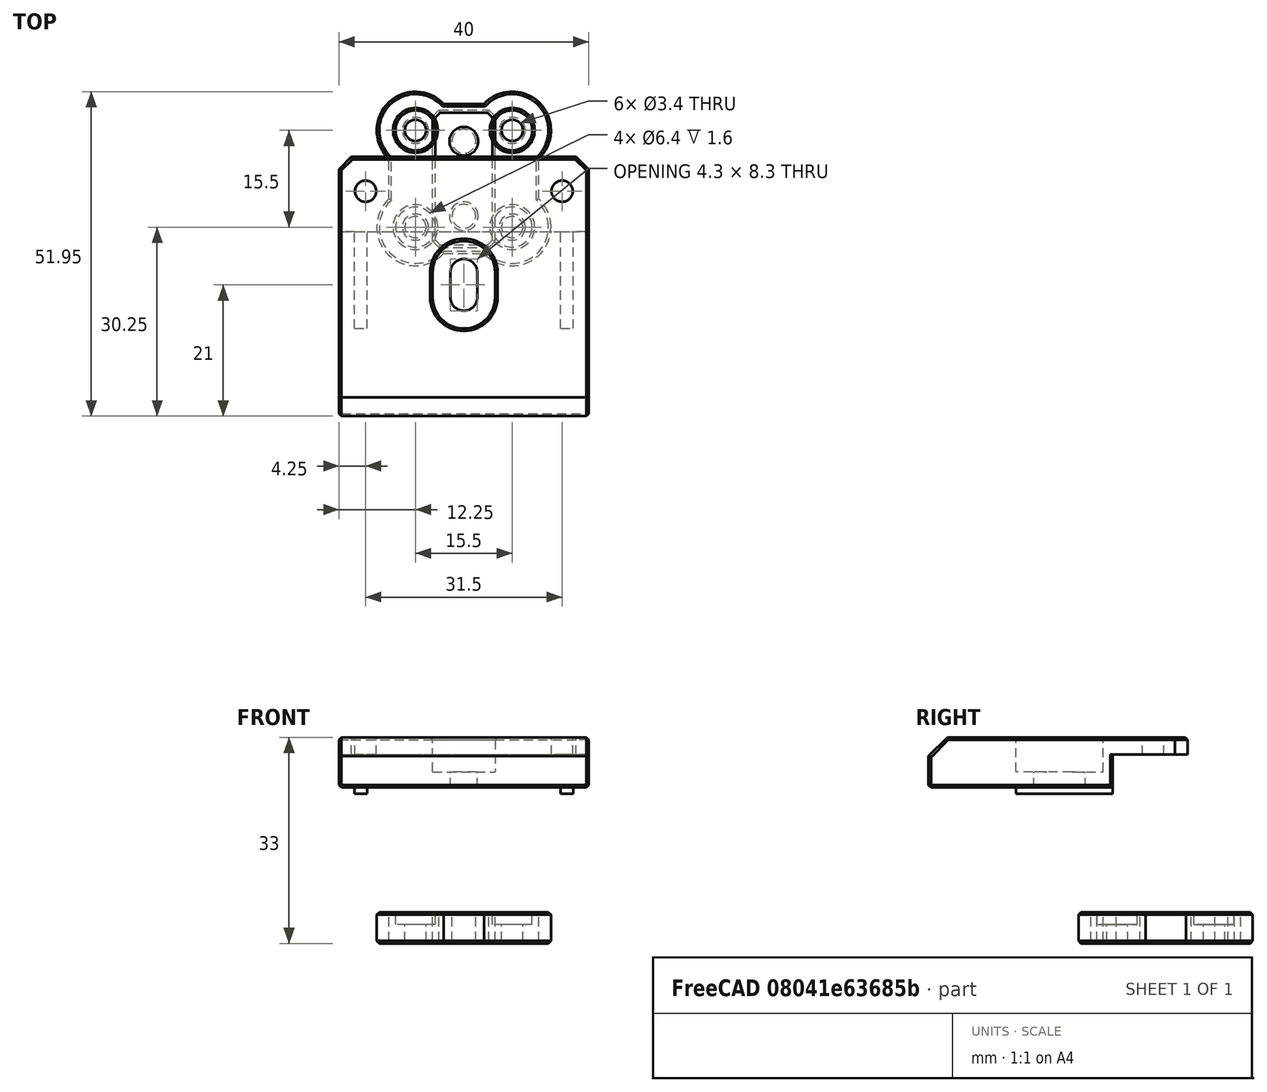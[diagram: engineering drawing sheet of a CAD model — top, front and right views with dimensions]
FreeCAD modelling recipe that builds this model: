
FCSTD DOCUMENT  (FreeCAD 0.19R24291 (Git))
Label: panel-mount-connector-wider
License: Other
LicenseURL: GPL3
objects: Part::Cylinder×18, Part::MultiFuse×6, Part::Cut×4, Part::Refine×4, Part::Chamfer×4, Part::Feature×4, Part::Box×2
note: 42 computed .brp shape members not serialized (recipe doc carries the construction recipe); baked Part::Feature solids carry a one-line shape summary decoded from their .brp

FEATURE [Part::Cylinder] Cylinder
  Angle = 360
  AttacherType = Attacher::AttachEngine3D
  Height = 10
  Placement = pos=(7.75,7.75,0) rot=(0,0,1;0rad)
  Radius = 1.7
FEATURE [Part::Cylinder] Cylinder001
  Angle = 360
  AttacherType = Attacher::AttachEngine3D
  Height = 10
  Placement = pos=(-7.75,7.75,0) rot=(0,0,1;0rad)
  Radius = 1.7
FEATURE [Part::Cylinder] Cylinder002
  Angle = 360
  AttacherType = Attacher::AttachEngine3D
  Height = 10
  Placement = pos=(7.75,-7.75,0) rot=(0,0,1;0rad)
  Radius = 1.7
FEATURE [Part::Cylinder] Cylinder003
  Angle = 360
  AttacherType = Attacher::AttachEngine3D
  Height = 10
  Placement = pos=(-7.75,-7.75,0) rot=(0,0,1;0rad)
  Radius = 1.7
FEATURE [Part::Cylinder] Cylinder005
  Angle = 360
  AttacherType = Attacher::AttachEngine3D
  Height = 5
  Placement = pos=(7.75,-7.75,0) rot=(0,0,1;0rad)
  Radius = 6.2
FEATURE [Part::Cylinder] Cylinder006
  Angle = 360
  AttacherType = Attacher::AttachEngine3D
  Height = 5
  Placement = pos=(-7.75,7.75,0) rot=(0,0,1;0rad)
  Radius = 6.2
FEATURE [Part::Cylinder] Cylinder007
  Angle = 360
  AttacherType = Attacher::AttachEngine3D
  Height = 5
  Placement = pos=(7.75,7.75,0) rot=(0,0,1;0rad)
  Radius = 6.2
FEATURE [Part::Box] Box  label="Cube"
  AttacherType = Attacher::AttachEngine3D
  Height = 5
  Length = 24
  Placement = pos=(-12,-12,0) rot=(0,0,1;0rad)
  Width = 24
FEATURE [Part::Cylinder] Cylinder008
  Angle = 360
  AttacherType = Attacher::AttachEngine3D
  Height = 10
  Placement = pos=(-7.75,-7.75,0) rot=(0,0,1;0rad)
  Radius = 3.2
FEATURE [Part::Cylinder] Cylinder009
  Angle = 360
  AttacherType = Attacher::AttachEngine3D
  Height = 10
  Placement = pos=(7.75,7.75,0) rot=(0,0,1;0rad)
  Radius = 3.2
FEATURE [Part::Cylinder] Cylinder010
  Angle = 360
  AttacherType = Attacher::AttachEngine3D
  Height = 10
  Placement = pos=(-7.75,7.75,0) rot=(0,0,1;0rad)
  Radius = 3.2
FEATURE [Part::Cylinder] Cylinder011
  Angle = 360
  AttacherType = Attacher::AttachEngine3D
  Height = 10
  Placement = pos=(7.75,-7.75,0) rot=(0,0,1;0rad)
  Radius = 3.2
FEATURE [Part::MultiFuse] Fusion
  Placement = pos=(0,0,3) rot=(0,0,1;0rad)
  Shapes = -> [Cylinder011,Cylinder010,Cylinder009,Cylinder008]
FEATURE [Part::Cylinder] Cylinder004
  Angle = 360
  AttacherType = Attacher::AttachEngine3D
  Height = 5
  Placement = pos=(-7.75,-7.75,0) rot=(0,0,1;0rad)
  Radius = 6.2
FEATURE [Part::MultiFuse] Fusion001
  Shapes = -> [Cylinder004,Cylinder005,Cylinder006,Cylinder007,Box]
FEATURE [Part::Cut] Cut
  Base = -> Fusion001
  Tool = -> Fusion
FEATURE [Part::MultiFuse] Fusion002
  Shapes = -> [Cylinder,Cylinder001,Cylinder002,Cylinder003]
FEATURE [Part::Cut] Cut001
  Base = -> Cut
  Tool = -> Fusion002
FEATURE [Part::Refine] Cut001001
  Source = -> Cut001
FEATURE [Part::Chamfer] Chamfer
  Base = -> Cut001001
  Edges = 14 edges r=0.4: [Edge3,Edge5,Edge8,Edge11,Edge16,Edge26,Edge32,Edge37,Edge42,Edge47,Edge49,Edge50,Edge51,Edge52]
FEATURE [Part::Chamfer] Chamfer001
  Base = -> Chamfer
  Edges = 14 edges r=0.4: [Edge2,Edge5,Edge6,Edge13,Edge14,Edge15,Edge16,Edge17,Edge18,Edge19,Edge20,Edge21,Edge22,Edge23]
FEATURE [Part::Feature] Cut001002
  Placement = pos=(0,-23,25) rot=(0,0,1;0rad)
  shape: bbox 40 x 41.5 x 9 mm, 50 faces (baked)
FEATURE [Part::Cylinder] Cylinder012
  Angle = 360
  AttacherType = Attacher::AttachEngine3D
  Height = 2.75
  Placement = pos=(-15,-2,30.25) rot=(0,0,1;0rad)
  Radius = 4
FEATURE [Part::Cylinder] Cylinder013
  Angle = 360
  AttacherType = Attacher::AttachEngine3D
  Height = 2.75
  Placement = pos=(15,-2,30.25) rot=(0,0,1;0rad)
  Radius = 4
FEATURE [Part::Cylinder] Cylinder014
  Angle = 360
  AttacherType = Attacher::AttachEngine3D
  Height = 2.75
  Placement = pos=(15.75,-2,30.25) rot=(0,0,1;0rad)
  Radius = 1.7
FEATURE [Part::Cylinder] Cylinder015
  Angle = 360
  AttacherType = Attacher::AttachEngine3D
  Height = 2.75
  Placement = pos=(-15.75,-2,30.25) rot=(0,0,1;0rad)
  Radius = 1.7
FEATURE [Part::MultiFuse] Fusion003
  Shapes = -> [Cylinder013,Cylinder012,Cut001002]
FEATURE [Part::MultiFuse] Fusion004
  Shapes = -> [Cylinder015,Cylinder014]
FEATURE [Part::Cut] Cut001003
  Base = -> Fusion003
  Tool = -> Fusion004
FEATURE [Part::Box] Box001  label="Cube001"
  AttacherType = Attacher::AttachEngine3D
  Height = 5
  Length = 10
  Placement = pos=(-5,-11,0) rot=(0,0,1;0rad)
  Width = 22
FEATURE [Part::Cylinder] Cylinder016
  Angle = 360
  AttacherType = Attacher::AttachEngine3D
  Height = 10
  Placement = pos=(0,6,0) rot=(0,0,1;0rad)
  Radius = 1.9
FEATURE [Part::Cylinder] Cylinder017
  Angle = 360
  AttacherType = Attacher::AttachEngine3D
  Height = 10
  Placement = pos=(0,-6,0) rot=(0,0,1;0rad)
  Radius = 1.9
FEATURE [Part::MultiFuse] Fusion005
  Shapes = -> [Cylinder016,Cylinder017]
FEATURE [Part::Chamfer] Chamfer002
  Base = -> Box001
  Edges = 4 edges r=1: [Edge1,Edge3,Edge5,Edge7]
FEATURE [Part::Cut] Cut001004
  Base = -> Chamfer002
  Tool = -> Fusion005
FEATURE [Part::Chamfer] Chamfer003
  Base = -> Cut001004
  Edges = 20 edges r=0.4: [Edge1,Edge3,Edge5,Edge6,Edge7,Edge8,Edge9,Edge10,Edge11,Edge12,Edge13,Edge14,Edge16,Edge17,Edge18,Edge19,Edge20,Edge21,Edge22,Edge23]
FEATURE [Part::Refine] Chamfer003001
  Source = -> Chamfer003
FEATURE [Part::Refine] Cut001003001
  Source = -> Cut001003
FEATURE [Part::Refine] Chamfer001001
  Source = -> Chamfer001
FEATURE [Part::Feature] Chamfer001001001
  shape: bbox 27.9 x 27.9 x 5 mm, 50 faces (baked)
FEATURE [Part::Feature] Cut001003001001
  shape: bbox 40 x 41.5 x 9 mm, 50 faces (baked)
FEATURE [Part::Feature] Chamfer003001001
  shape: bbox 10 x 22 x 5 mm, 32 faces (baked)
